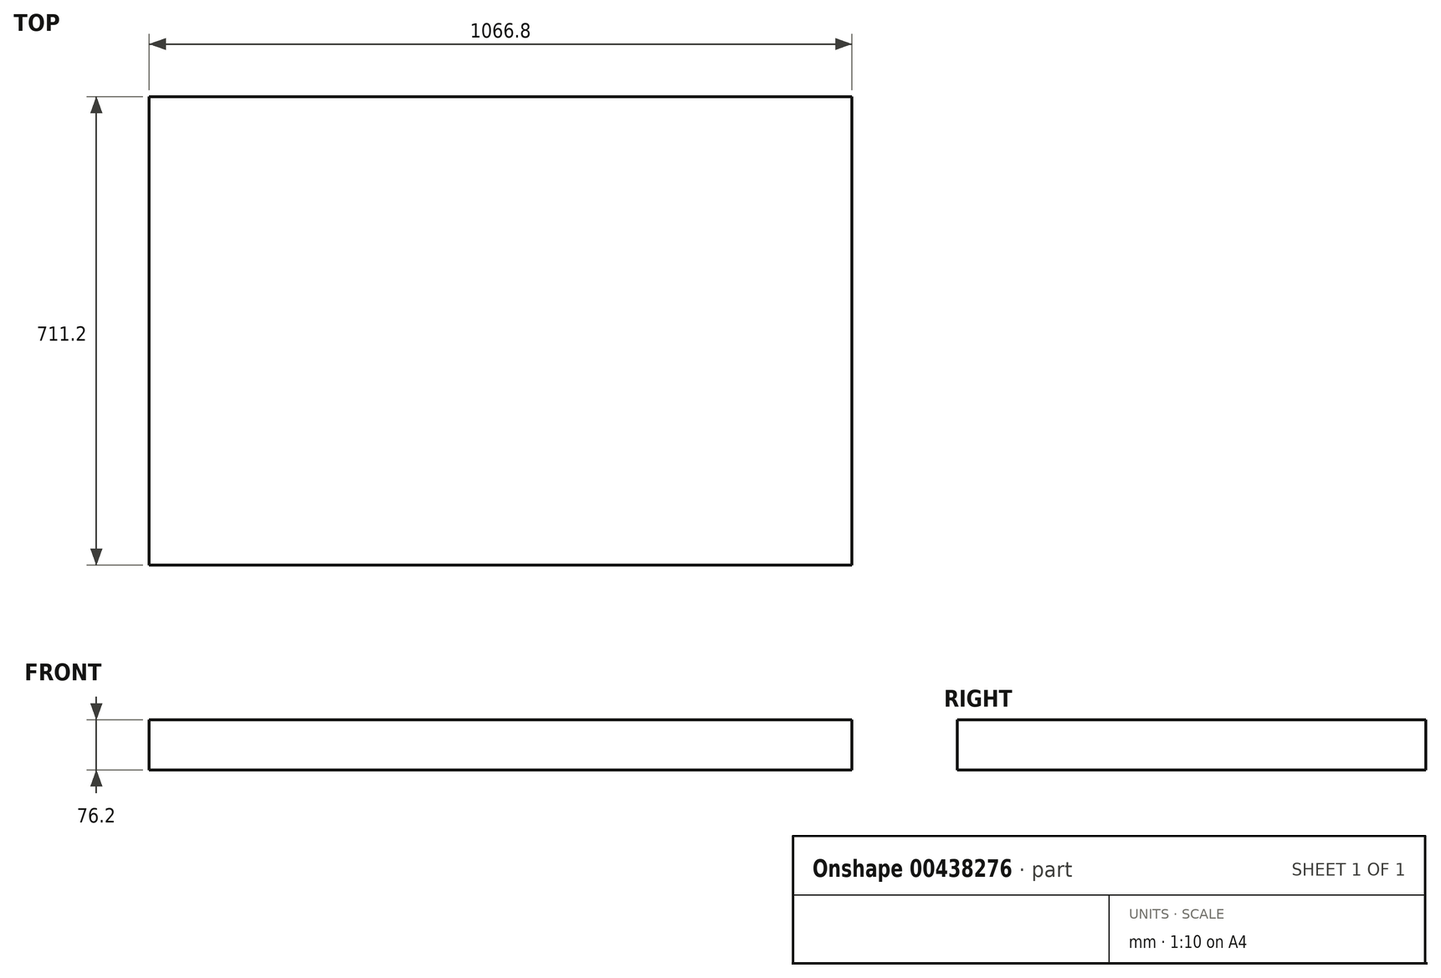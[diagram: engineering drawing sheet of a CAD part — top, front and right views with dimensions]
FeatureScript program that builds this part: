
annotation { "Feature Type Name" : "Feature", "Feature Type Description" : "" }
export const myFeature = defineFeature(function(context is Context, id is Id, definition is map)
    precondition{}
    {
        {
            var Q0;
            Q0=qCreatedBy(makeId("Front.planeOp"),FACE);
            var sketch = newSketch(context, id + "F0", { "sketchPlane" : qUnion([Q0])});
            skLineSegment(sketch, "E0.bottom", {"start": v(-514.85, 38.1) * mm, "end": v(551.95, 38.1) * mm});
            skLineSegment(sketch, "E0.top", {"start": v(-514.85, -38.1) * mm, "end": v(551.95, -38.1) * mm});
            skLineSegment(sketch, "E0.left", {"start": v(-514.85, 38.1) * mm, "end": v(-514.85, -38.1) * mm});
            skLineSegment(sketch, "E0.right", {"start": v(551.95, 38.1) * mm, "end": v(551.95, -38.1) * mm});
            skPoint(sketch, "E0.middle", {"position": v(18.55, 0) * mm});
            skSolve(sketch);
        }
        {
            var Q0;
            Q0 = qSketchRegion(id + "F0", true);
            extrude(context, id + "F1", {"entities" : qUnion([Q0]), "endBound" : BoundingType.SYMMETRIC, "depth" : 711.2 * mm});
        }
    });
